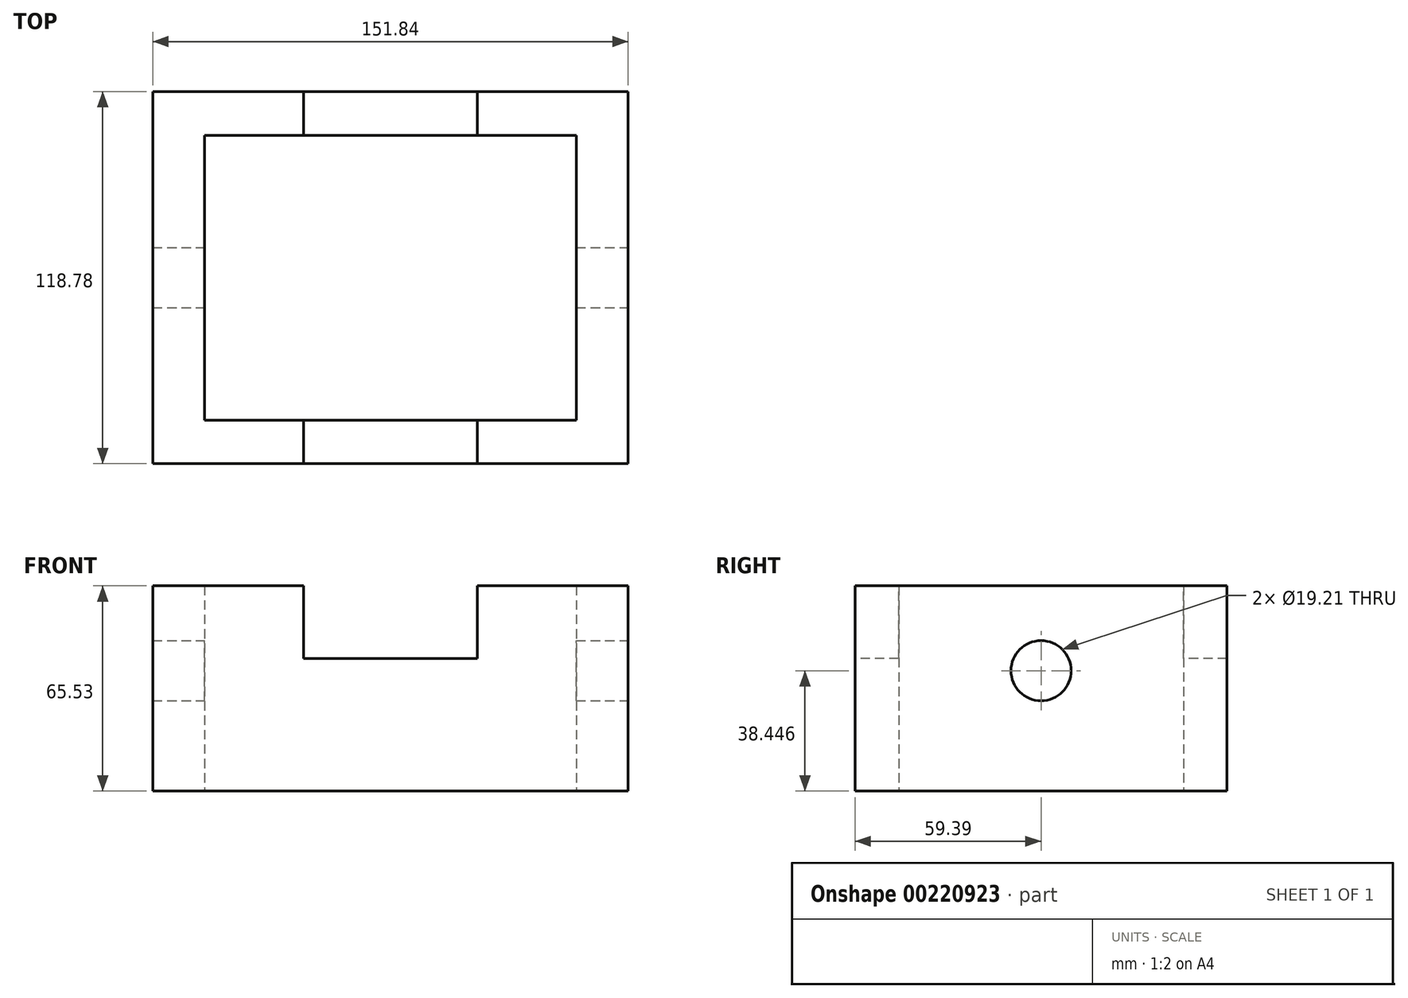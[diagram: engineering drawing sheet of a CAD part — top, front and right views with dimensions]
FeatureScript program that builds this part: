
annotation { "Feature Type Name" : "Feature", "Feature Type Description" : "" }
export const myFeature = defineFeature(function(context is Context, id is Id, definition is map)
    precondition{}
    {
        {
            var Q0;
            Q0=qCreatedBy(makeId("Top.planeOp"),FACE);
            var sketch = newSketch(context, id + "F0", { "sketchPlane" : qUnion([Q0])});
            skLineSegment(sketch, "E0.bottom", {"start": v(-75.92, 59.4) * mm, "end": v(75.92, 59.4) * mm});
            skLineSegment(sketch, "E0.top", {"start": v(-75.92, -59.4) * mm, "end": v(75.92, -59.4) * mm});
            skLineSegment(sketch, "E0.left", {"start": v(-75.92, 59.4) * mm, "end": v(-75.92, -59.4) * mm});
            skLineSegment(sketch, "E0.right", {"start": v(75.92, 59.4) * mm, "end": v(75.92, -59.4) * mm});
            skPoint(sketch, "E0.middle", {"position": v(0, 0) * mm});
            skLineSegment(sketch, "E1.bottom", {"start": v(-59.35, 45.48) * mm, "end": v(59.35, 45.48) * mm});
            skLineSegment(sketch, "E1.top", {"start": v(-59.35, -45.48) * mm, "end": v(59.35, -45.48) * mm});
            skLineSegment(sketch, "E1.left", {"start": v(-59.35, 45.48) * mm, "end": v(-59.35, -45.48) * mm});
            skLineSegment(sketch, "E1.right", {"start": v(59.35, 45.48) * mm, "end": v(59.35, -45.48) * mm});
            skSolve(sketch);
        }
        {
            var Q0;
            Q0=makeQuery(id+"F0.imprint","IMPRINT",FACE,{"disambiguationData":[TD([[makeQuery(id+"F0.imprint","IMPRINT",EDGE,{"derivedFrom":sQuery(id+"F0.wireOp",EDGE,"E0.bottom")}),-1.0]])]});
            extrude(context, id + "F1", {"entities" : qUnion([Q0]), "depth" : 50.8 * mm});
        }
        {
            var Q0;
            Q0=makeQuery(id+"F0.imprint","IMPRINT",FACE,{"disambiguationData":[TD([[makeQuery(id+"F0.imprint","IMPRINT",EDGE,{"derivedFrom":sQuery(id+"F0.wireOp",EDGE,"E0.bottom")}),-1.0]])]});
            extrude(context, id + "F2", {"entities" : qUnion([Q0]), "operationType" : NewBodyOperationType.ADD, "depth" : 65.53 * mm});
        }
        {
            var Q0;
            {var subQ0=sQuery(id+"F0.wireOp",EDGE,"E0.top");Q0=makeQuery(id+"F2.boolean.opBoolean","MERGE",FACE,{"derivedFrom":[makeQuery(id+"F1.opExtrude","SWEPT_FACE",FACE,{"disambiguationData":[OSD([subQ0])]}),makeQuery(id+"F2.opExtrude","SWEPT_FACE",FACE,{"disambiguationData":[OSD([subQ0])]})]});}
            var sketch = newSketch(context, id + "F3", { "sketchPlane" : qUnion([Q0])});
            skLineSegment(sketch, "E2.bottom", {"start": v(-27.7, 65.53) * mm, "end": v(27.7, 65.53) * mm});
            skLineSegment(sketch, "E2.top", {"start": v(-27.7, 42.3) * mm, "end": v(27.7, 42.3) * mm});
            skLineSegment(sketch, "E2.left", {"start": v(-27.7, 65.53) * mm, "end": v(-27.7, 42.3) * mm});
            skLineSegment(sketch, "E2.right", {"start": v(27.7, 65.53) * mm, "end": v(27.7, 42.3) * mm});
            skPoint(sketch, "E2.middle", {"position": v(0, 53.92) * mm});
            skSolve(sketch);
        }
        {
            var Q0;
            Q0=makeQuery(id+"F3.imprint","IMPRINT",FACE,{"disambiguationData":[TD([[makeQuery(id+"F3.imprint","IMPRINT",EDGE,{"derivedFrom":sQuery(id+"F3.wireOp",EDGE,"E2.bottom")}),-1.0]])]});
            extrude(context, id + "F4", {"entities" : qUnion([Q0]), "operationType" : NewBodyOperationType.REMOVE, "endBound" : BoundingType.THROUGH_ALL, "oppositeDirection" : true, "depth" : 25.4 * mm});
        }
        {
            var Q0;
            {var subQ0=sQuery(id+"F0.wireOp",EDGE,"E0.right");Q0=makeQuery(id+"F2.boolean.opBoolean","MERGE",FACE,{"derivedFrom":[makeQuery(id+"F1.opExtrude","SWEPT_FACE",FACE,{"disambiguationData":[OSD([subQ0])]}),makeQuery(id+"F2.opExtrude","SWEPT_FACE",FACE,{"disambiguationData":[OSD([subQ0])]})]});}
            var sketch = newSketch(context, id + "F5", { "sketchPlane" : qUnion([Q0])});
            skCircle(sketch, "E3", {"center": v(0, 38.45) * mm, "radius": 9.6 * mm});
            skSolve(sketch);
        }
        {
            var Q0;
            Q0=makeQuery(id+"F5.imprint","IMPRINT",FACE,{"disambiguationData":[TD([[makeQuery(id+"F5.imprint","IMPRINT",EDGE,{"derivedFrom":sQuery(id+"F5.wireOp",EDGE,"E3")}),1.0]])]});
            extrude(context, id + "F6", {"entities" : qUnion([Q0]), "operationType" : NewBodyOperationType.REMOVE, "endBound" : BoundingType.THROUGH_ALL, "oppositeDirection" : true, "depth" : 25.4 * mm});
        }
    });
